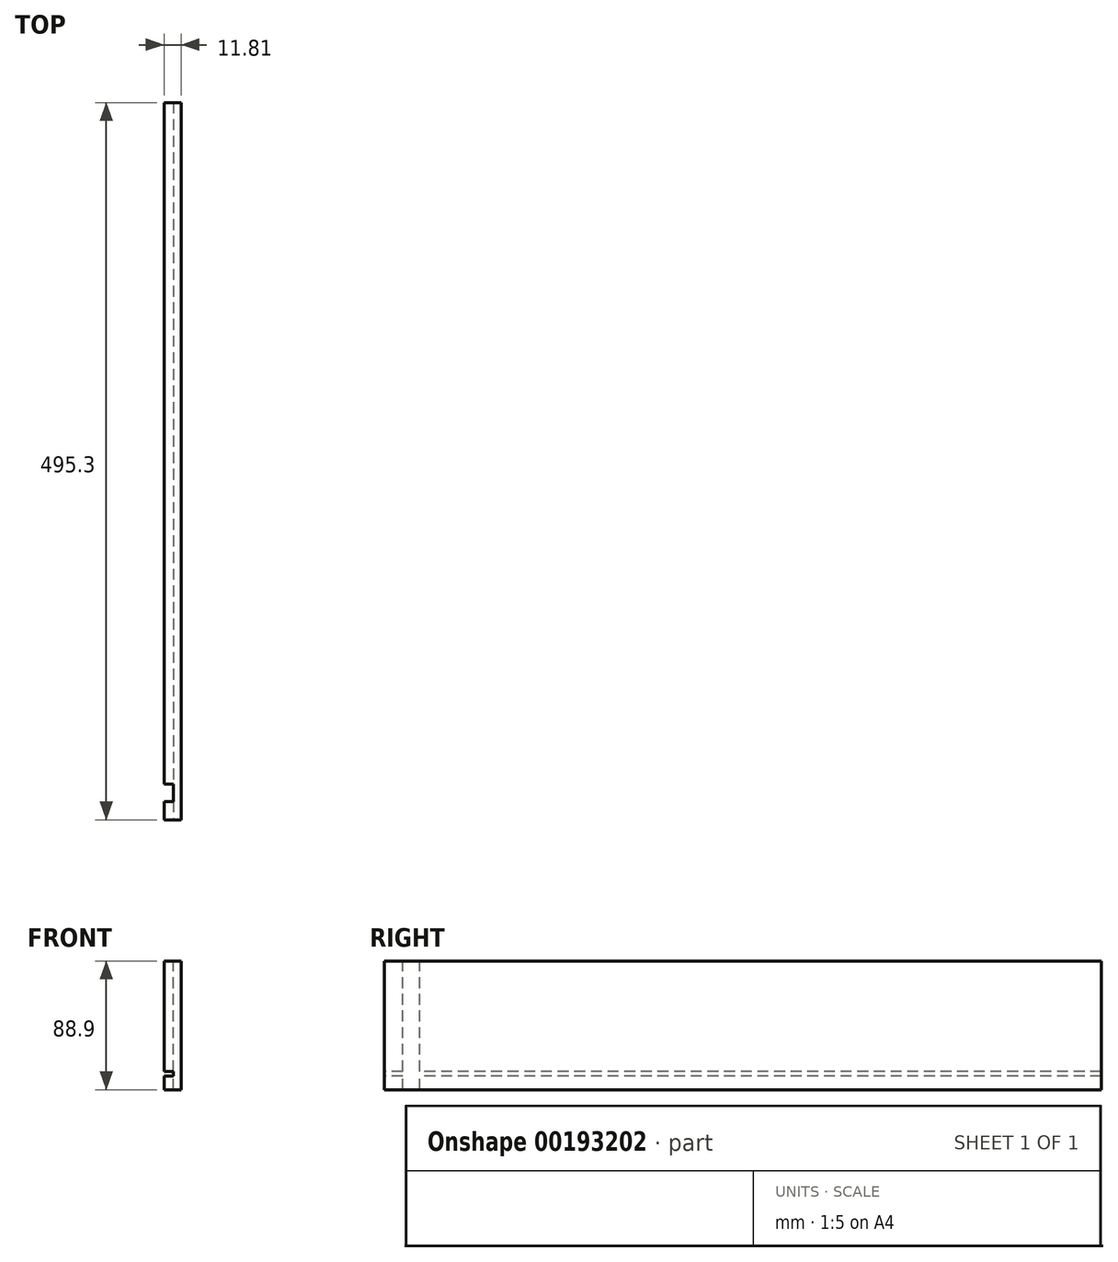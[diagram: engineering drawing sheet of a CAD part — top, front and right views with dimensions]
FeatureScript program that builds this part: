
annotation { "Feature Type Name" : "Feature", "Feature Type Description" : "" }
export const myFeature = defineFeature(function(context is Context, id is Id, definition is map)
    precondition{}
    {
        {
            var Q0;
            Q0=qCreatedBy(makeId("Front.planeOp"),FACE);
            var sketch = newSketch(context, id + "F0", { "sketchPlane" : qUnion([Q0])});
            skLineSegment(sketch, "E0.bottom", {"start": v(0, 0) * mm, "end": v(11.81, 0) * mm});
            skLineSegment(sketch, "E0.top", {"start": v(0, -88.9) * mm, "end": v(11.81, -88.9) * mm});
            skLineSegment(sketch, "E0.left", {"start": v(0, 0) * mm, "end": v(0, -76.2) * mm});
            skLineSegment(sketch, "E0.right", {"start": v(11.81, 0) * mm, "end": v(11.81, -88.9) * mm});
            skLineSegment(sketch, "E1.bottom", {"start": v(0, -76.2) * mm, "end": v(6.35, -76.2) * mm});
            skLineSegment(sketch, "E1.top", {"start": v(0, -79.38) * mm, "end": v(6.35, -79.38) * mm});
            skLineSegment(sketch, "E1.right", {"start": v(6.35, -76.2) * mm, "end": v(6.35, -79.38) * mm});
            skLineSegment(sketch, "E2.trimOffspring", {"start": v(0, -79.38) * mm, "end": v(0, -88.9) * mm});
            skSolve(sketch);
        }
        {
            var Q0;
            Q0 = qSketchRegion(id + "F0", true);
            extrude(context, id + "F1", {"entities" : qUnion([Q0]), "oppositeDirection" : true, "depth" : 495.3 * mm});
        }
        {
            var Q0;
            Q0=makeQuery(id+"F1.opExtrude","SWEPT_FACE",FACE,{"disambiguationData":[OSD([sQuery(id+"F0.wireOp",EDGE,"E0.bottom")])]});
            var sketch = newSketch(context, id + "F2", { "sketchPlane" : qUnion([Q0])});
            skLineSegment(sketch, "E3.bottom", {"start": v(0, 12.7) * mm, "end": v(6.35, 12.7) * mm});
            skLineSegment(sketch, "E3.top", {"start": v(0, 24.51) * mm, "end": v(6.35, 24.51) * mm});
            skLineSegment(sketch, "E3.left", {"start": v(0, 12.7) * mm, "end": v(0, 24.51) * mm});
            skLineSegment(sketch, "E3.right", {"start": v(6.35, 12.7) * mm, "end": v(6.35, 24.51) * mm});
            skSolve(sketch);
        }
        {
            var Q0;
            Q0 = qSketchRegion(id + "F2", true);
            extrude(context, id + "F3", {"entities" : qUnion([Q0]), "operationType" : NewBodyOperationType.REMOVE, "endBound" : BoundingType.THROUGH_ALL, "oppositeDirection" : true, "depth" : 25.4 * mm});
        }
    });
